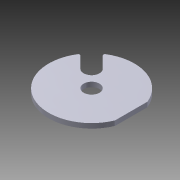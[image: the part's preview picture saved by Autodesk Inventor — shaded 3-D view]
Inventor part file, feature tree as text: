
AUTODESK INVENTOR PART (.ipt)
format: ipt  version: 2015 (Build 190159000, 159)  size: 102,400 bytes
history: native  units: mm
features: extrude x1, sketch x1
ambient origin geometry x8: Origin, YZ Plane, XZ Plane, XY Plane, X Axis, Y Axis, Z Axis, Center Point
bodies: Body1 (feature_tree)
feature tree (2):
  extrude  "Extrusion3"  Depth=20.0mm
  sketch  "Sketch1"  dims[d0=108.0mm d1=20.0mm d4=20.0mm d12=50.0mm d13=2.0mm d14=54.0mm d15=54.0mm d16=20.0mm d17=6.0mm d18=0.0mm d19=45.0deg d21=10.0mm d22=30.0mm]
